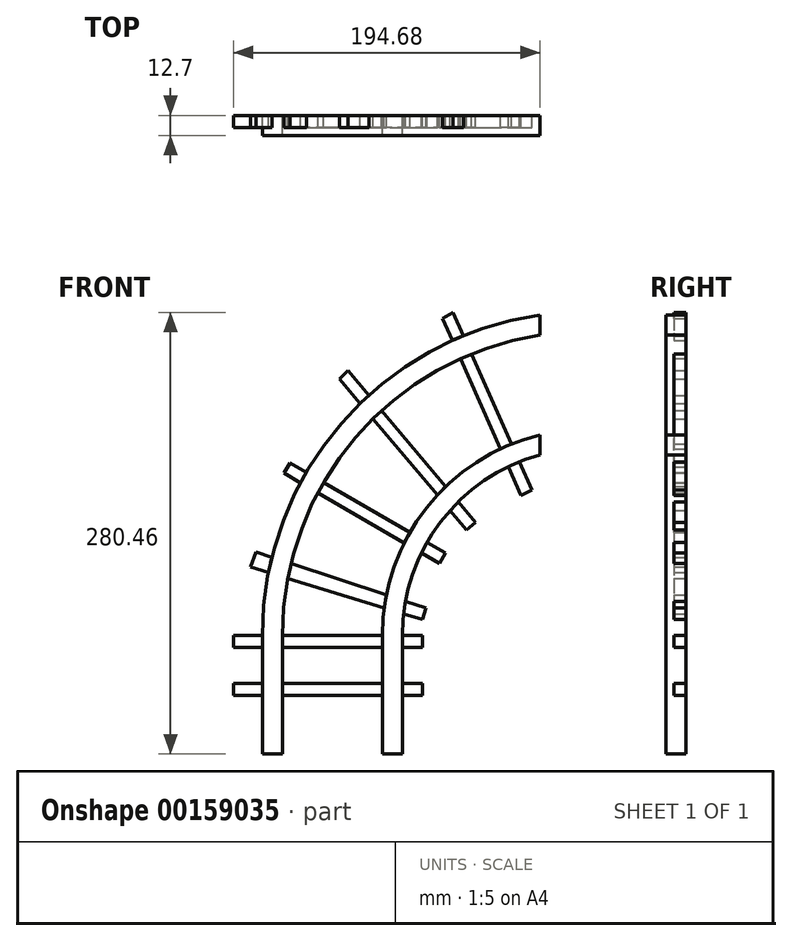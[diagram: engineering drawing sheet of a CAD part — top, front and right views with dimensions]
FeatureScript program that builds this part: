
annotation { "Feature Type Name" : "Feature", "Feature Type Description" : "" }
export const myFeature = defineFeature(function(context is Context, id is Id, definition is map)
    precondition{}
    {
        {
            var Q0;
            Q0=qCreatedBy(makeId("Front.planeOp"),FACE);
            var sketch = newSketch(context, id + "F0", { "sketchPlane" : qUnion([Q0])});
            skLineSegment(sketch, "E0", {"start": v(-53.08, 0) * mm, "end": v(-40.38, 0) * mm});
            skLineSegment(sketch, "E1", {"start": v(-40.38, 0) * mm, "end": v(-40.38, -75.5) * mm});
            skLineSegment(sketch, "E2", {"start": v(-40.38, -75.5) * mm, "end": v(-53.08, -75.5) * mm});
            skLineSegment(sketch, "E3", {"start": v(-53.08, -75.5) * mm, "end": v(-53.08, 0) * mm});
            skLineSegment(sketch, "E4", {"start": v(23.12, 0) * mm, "end": v(35.82, 0) * mm});
            skLineSegment(sketch, "E5", {"start": v(35.82, 0) * mm, "end": v(35.82, -75.5) * mm});
            skLineSegment(sketch, "E6", {"start": v(35.82, -75.5) * mm, "end": v(23.12, -75.5) * mm});
            skLineSegment(sketch, "E7", {"start": v(23.12, -75.5) * mm, "end": v(23.12, 0) * mm});
            skArc(sketch, "E8", {"start": v(123.26, 114.48) * mm, "mid": v(60.18, 72.03) * mm, "end": v(35.82, 0) * mm});
            skArc(sketch, "E9", {"start": v(123.26, 127.18) * mm, "mid": v(51.16, 80.94) * mm, "end": v(23.12, 0) * mm});
            skArc(sketch, "E10", {"start": v(123.26, 190.68) * mm, "mid": v(6.14, 125.64) * mm, "end": v(-40.38, 0) * mm});
            skArc(sketch, "E11", {"start": v(123.26, 203.38) * mm, "mid": v(-2.85, 134.6) * mm, "end": v(-53.08, 0) * mm});
            skLineSegment(sketch, "E12", {"start": v(123.26, 203.38) * mm, "end": v(123.26, 190.68) * mm});
            skLineSegment(sketch, "E13", {"start": v(123.26, 127.18) * mm, "end": v(123.26, 114.48) * mm});
            skLineSegment(sketch, "E14", {"start": v(-71.42, -30.48) * mm, "end": v(-71.42, -38.1) * mm});
            skLineSegment(sketch, "E15", {"start": v(-71.42, -38.1) * mm, "end": v(48.77, -38.1) * mm});
            skLineSegment(sketch, "E16", {"start": v(48.77, -38.1) * mm, "end": v(48.77, -30.48) * mm});
            skLineSegment(sketch, "E17", {"start": v(48.77, -30.48) * mm, "end": v(-71.42, -30.48) * mm});
            skLineSegment(sketch, "E18", {"start": v(-71.42, 0) * mm, "end": v(-71.42, -7.62) * mm});
            skLineSegment(sketch, "E19", {"start": v(-71.42, -7.62) * mm, "end": v(48.77, -7.62) * mm});
            skLineSegment(sketch, "E20", {"start": v(48.77, -7.62) * mm, "end": v(48.77, 0) * mm});
            skLineSegment(sketch, "E21", {"start": v(48.77, 0) * mm, "end": v(-71.42, 0) * mm});
            skLineSegment(sketch, "E22", {"start": v(-57.02, 52.83) * mm, "end": v(-60.61, 43.26) * mm});
            skLineSegment(sketch, "E23", {"start": v(-60.61, 43.26) * mm, "end": v(48.67, 9.97) * mm});
            skLineSegment(sketch, "E24", {"start": v(48.67, 9.97) * mm, "end": v(50.89, 17.26) * mm});
            skLineSegment(sketch, "E25", {"start": v(-57.02, 52.83) * mm, "end": v(50.89, 17.26) * mm});
            skLineSegment(sketch, "E26", {"start": v(-35.6, 109.54) * mm, "end": v(-39.43, 102.95) * mm});
            skLineSegment(sketch, "E27", {"start": v(-39.43, 102.95) * mm, "end": v(59.36, 45.68) * mm});
            skLineSegment(sketch, "E28", {"start": v(59.36, 45.68) * mm, "end": v(63.18, 52.28) * mm});
            skLineSegment(sketch, "E29", {"start": v(63.18, 52.28) * mm, "end": v(-35.6, 109.54) * mm});
            skLineSegment(sketch, "E30", {"start": v(-4.06, 162.77) * mm, "end": v(1.23, 168.25) * mm});
            skLineSegment(sketch, "E31", {"start": v(-4.06, 162.77) * mm, "end": v(76.6, 66.78) * mm});
            skLineSegment(sketch, "E32", {"start": v(76.6, 66.78) * mm, "end": v(82.43, 71.69) * mm});
            skLineSegment(sketch, "E33", {"start": v(82.43, 71.69) * mm, "end": v(1.23, 168.25) * mm});
            skLineSegment(sketch, "E34", {"start": v(61.48, 201.09) * mm, "end": v(68.05, 204.95) * mm});
            skLineSegment(sketch, "E35", {"start": v(68.05, 204.95) * mm, "end": v(118.1, 92.17) * mm});
            skLineSegment(sketch, "E36", {"start": v(61.48, 201.09) * mm, "end": v(111.28, 88.77) * mm});
            skLineSegment(sketch, "E37", {"start": v(111.28, 88.77) * mm, "end": v(118.1, 92.17) * mm});
            skSolve(sketch);
        }
        {
            var Q0;
            {var subQ0=sQuery(id+"F0.wireOp",EDGE,"E12");Q0=makeQuery(id+"F0.imprint","IMPRINT",FACE,{"disambiguationData":[TD([[makeQuery(id+"F0.imprint","IMPRINT",EDGE,{"derivedFrom":subQ0}),-1.0]])]});}
            var Q1;
            {var subQ0=sQuery(id+"F0.wireOp",EDGE,"E35");var subQ1=sQuery(id+"F0.wireOp",EDGE,"E10");var subQ2=makeQuery(id+"F0.imprint","INTERSECT",VERTEX,{"derivedFrom":[subQ1,subQ0]});Q1=makeQuery(id+"F0.imprint","IMPRINT",FACE,{"disambiguationData":[TD([[makeQuery(id+"F0.imprint","IMPRINT",EDGE,{"disambiguationData":[TD([[subQ2,-1.0]])],"derivedFrom":subQ1}),-1.0]])]});}
            var Q2;
            {var subQ0=sQuery(id+"F0.wireOp",EDGE,"E36");var subQ1=sQuery(id+"F0.wireOp",EDGE,"E10");var subQ2=makeQuery(id+"F0.imprint","INTERSECT",VERTEX,{"derivedFrom":[subQ1,subQ0]});Q2=makeQuery(id+"F0.imprint","IMPRINT",FACE,{"disambiguationData":[TD([[makeQuery(id+"F0.imprint","IMPRINT",EDGE,{"disambiguationData":[TD([[subQ2,-1.0]])],"derivedFrom":subQ1}),-1.0]])]});}
            var Q3;
            {var subQ0=sQuery(id+"F0.wireOp",EDGE,"E33");var subQ1=sQuery(id+"F0.wireOp",EDGE,"E10");var subQ2=makeQuery(id+"F0.imprint","INTERSECT",VERTEX,{"derivedFrom":[subQ1,subQ0]});Q3=makeQuery(id+"F0.imprint","IMPRINT",FACE,{"disambiguationData":[TD([[makeQuery(id+"F0.imprint","IMPRINT",EDGE,{"disambiguationData":[TD([[subQ2,-1.0]])],"derivedFrom":subQ1}),-1.0]])]});}
            var Q4;
            {var subQ0=sQuery(id+"F0.wireOp",EDGE,"E31");var subQ1=sQuery(id+"F0.wireOp",EDGE,"E10");var subQ2=makeQuery(id+"F0.imprint","INTERSECT",VERTEX,{"derivedFrom":[subQ1,subQ0]});Q4=makeQuery(id+"F0.imprint","IMPRINT",FACE,{"disambiguationData":[TD([[makeQuery(id+"F0.imprint","IMPRINT",EDGE,{"disambiguationData":[TD([[subQ2,-1.0]])],"derivedFrom":subQ1}),-1.0]])]});}
            var Q5;
            {var subQ0=sQuery(id+"F0.wireOp",EDGE,"E27");var subQ1=sQuery(id+"F0.wireOp",EDGE,"E10");var subQ2=makeQuery(id+"F0.imprint","INTERSECT",VERTEX,{"derivedFrom":[subQ1,subQ0]});Q5=makeQuery(id+"F0.imprint","IMPRINT",FACE,{"disambiguationData":[TD([[makeQuery(id+"F0.imprint","IMPRINT",EDGE,{"disambiguationData":[TD([[subQ2,-1.0]])],"derivedFrom":subQ1}),-1.0]])]});}
            var Q6;
            {var subQ0=sQuery(id+"F0.wireOp",EDGE,"E29");var subQ1=sQuery(id+"F0.wireOp",EDGE,"E10");var subQ2=makeQuery(id+"F0.imprint","INTERSECT",VERTEX,{"derivedFrom":[subQ1,subQ0]});Q6=makeQuery(id+"F0.imprint","IMPRINT",FACE,{"disambiguationData":[TD([[makeQuery(id+"F0.imprint","IMPRINT",EDGE,{"disambiguationData":[TD([[subQ2,-1.0]])],"derivedFrom":subQ1}),-1.0]])]});}
            var Q7;
            {var subQ0=sQuery(id+"F0.wireOp",EDGE,"E25");var subQ1=sQuery(id+"F0.wireOp",EDGE,"E10");var subQ2=makeQuery(id+"F0.imprint","INTERSECT",VERTEX,{"derivedFrom":[subQ1,subQ0]});Q7=makeQuery(id+"F0.imprint","IMPRINT",FACE,{"disambiguationData":[TD([[makeQuery(id+"F0.imprint","IMPRINT",EDGE,{"disambiguationData":[TD([[subQ2,-1.0]])],"derivedFrom":subQ1}),-1.0]])]});}
            var Q8;
            {var subQ3=sQuery(id+"F0.wireOp",EDGE,"E23");var subQ5=sQuery(id+"F0.wireOp",EDGE,"E11");var subQ7=makeQuery(id+"F0.imprint","INTERSECT",VERTEX,{"derivedFrom":[subQ5,subQ3]});Q8=makeQuery(id+"F0.imprint","IMPRINT",FACE,{"disambiguationData":[TD([[makeQuery(id+"F0.imprint","IMPRINT",EDGE,{"disambiguationData":[TD([[subQ7,-1.0]])],"derivedFrom":subQ3}),-1.0]])]});}
            var Q9;
            {var subQ3=sQuery(id+"F0.wireOp",EDGE,"E19");var subQ5=sQuery(id+"F0.wireOp",EDGE,"E3");var subQ6=makeQuery(id+"F0.imprint","INTERSECT",VERTEX,{"derivedFrom":[subQ5,subQ3]});Q9=makeQuery(id+"F0.imprint","IMPRINT",FACE,{"disambiguationData":[TD([[makeQuery(id+"F0.imprint","IMPRINT",EDGE,{"disambiguationData":[TD([[subQ6,-1.0]])],"derivedFrom":subQ3}),1.0]])]});}
            var Q10;
            {var subQ0=sQuery(id+"F0.wireOp",EDGE,"E19");var subQ1=sQuery(id+"F0.wireOp",EDGE,"E1");var subQ2=makeQuery(id+"F0.imprint","INTERSECT",VERTEX,{"derivedFrom":[subQ1,subQ0]});Q10=makeQuery(id+"F0.imprint","IMPRINT",FACE,{"disambiguationData":[TD([[makeQuery(id+"F0.imprint","IMPRINT",EDGE,{"disambiguationData":[TD([[subQ2,-1.0]])],"derivedFrom":subQ1}),-1.0]])]});}
            var Q11;
            {var subQ0=sQuery(id+"F0.wireOp",EDGE,"E15");var subQ1=sQuery(id+"F0.wireOp",EDGE,"E1");var subQ2=makeQuery(id+"F0.imprint","INTERSECT",VERTEX,{"derivedFrom":[subQ1,subQ0]});Q11=makeQuery(id+"F0.imprint","IMPRINT",FACE,{"disambiguationData":[TD([[makeQuery(id+"F0.imprint","IMPRINT",EDGE,{"disambiguationData":[TD([[subQ2,1.0]])],"derivedFrom":subQ1}),-1.0]])]});}
            var Q12;
            {var subQ0=sQuery(id+"F0.wireOp",EDGE,"E2");Q12=makeQuery(id+"F0.imprint","IMPRINT",FACE,{"disambiguationData":[TD([[makeQuery(id+"F0.imprint","IMPRINT",EDGE,{"derivedFrom":subQ0}),-1.0]])]});}
            var Q13;
            {var subQ0=sQuery(id+"F0.wireOp",EDGE,"E6");Q13=makeQuery(id+"F0.imprint","IMPRINT",FACE,{"disambiguationData":[TD([[makeQuery(id+"F0.imprint","IMPRINT",EDGE,{"derivedFrom":subQ0}),-1.0]])]});}
            var Q14;
            {var subQ0=sQuery(id+"F0.wireOp",EDGE,"E17");var subQ1=sQuery(id+"F0.wireOp",EDGE,"E5");var subQ2=makeQuery(id+"F0.imprint","INTERSECT",VERTEX,{"derivedFrom":[subQ1,subQ0]});Q14=makeQuery(id+"F0.imprint","IMPRINT",FACE,{"disambiguationData":[TD([[makeQuery(id+"F0.imprint","IMPRINT",EDGE,{"disambiguationData":[TD([[subQ2,-1.0]])],"derivedFrom":subQ1}),-1.0]])]});}
            var Q15;
            {var subQ0=sQuery(id+"F0.wireOp",EDGE,"E19");var subQ1=sQuery(id+"F0.wireOp",EDGE,"E5");var subQ2=makeQuery(id+"F0.imprint","INTERSECT",VERTEX,{"derivedFrom":[subQ1,subQ0]});Q15=makeQuery(id+"F0.imprint","IMPRINT",FACE,{"disambiguationData":[TD([[makeQuery(id+"F0.imprint","IMPRINT",EDGE,{"disambiguationData":[TD([[subQ2,-1.0]])],"derivedFrom":subQ1}),-1.0]])]});}
            var Q16;
            {var subQ1=sQuery(id+"F0.wireOp",EDGE,"E5");var subQ3=sQuery(id+"F0.wireOp",EDGE,"E19");var subQ4=makeQuery(id+"F0.imprint","INTERSECT",VERTEX,{"derivedFrom":[subQ1,subQ3]});Q16=makeQuery(id+"F0.imprint","IMPRINT",FACE,{"disambiguationData":[TD([[makeQuery(id+"F0.imprint","IMPRINT",EDGE,{"disambiguationData":[TD([[subQ4,1.0]])],"derivedFrom":subQ3}),1.0]])]});}
            var Q17;
            {var subQ1=sQuery(id+"F0.wireOp",EDGE,"E8");var subQ3=sQuery(id+"F0.wireOp",EDGE,"E23");var subQ4=makeQuery(id+"F0.imprint","INTERSECT",VERTEX,{"derivedFrom":[subQ1,subQ3]});Q17=makeQuery(id+"F0.imprint","IMPRINT",FACE,{"disambiguationData":[TD([[makeQuery(id+"F0.imprint","IMPRINT",EDGE,{"disambiguationData":[TD([[subQ4,1.0]])],"derivedFrom":subQ3}),-1.0]])]});}
            var Q18;
            {var subQ0=sQuery(id+"F0.wireOp",EDGE,"E25");var subQ1=sQuery(id+"F0.wireOp",EDGE,"E8");var subQ2=makeQuery(id+"F0.imprint","INTERSECT",VERTEX,{"derivedFrom":[subQ1,subQ0]});Q18=makeQuery(id+"F0.imprint","IMPRINT",FACE,{"disambiguationData":[TD([[makeQuery(id+"F0.imprint","IMPRINT",EDGE,{"disambiguationData":[TD([[subQ2,-1.0]])],"derivedFrom":subQ1}),-1.0]])]});}
            var Q19;
            {var subQ0=sQuery(id+"F0.wireOp",EDGE,"E27");var subQ1=sQuery(id+"F0.wireOp",EDGE,"E8");var subQ2=makeQuery(id+"F0.imprint","INTERSECT",VERTEX,{"derivedFrom":[subQ1,subQ0]});Q19=makeQuery(id+"F0.imprint","IMPRINT",FACE,{"disambiguationData":[TD([[makeQuery(id+"F0.imprint","IMPRINT",EDGE,{"disambiguationData":[TD([[subQ2,-1.0]])],"derivedFrom":subQ1}),-1.0]])]});}
            var Q20;
            {var subQ0=sQuery(id+"F0.wireOp",EDGE,"E29");var subQ1=sQuery(id+"F0.wireOp",EDGE,"E8");var subQ2=makeQuery(id+"F0.imprint","INTERSECT",VERTEX,{"derivedFrom":[subQ1,subQ0]});Q20=makeQuery(id+"F0.imprint","IMPRINT",FACE,{"disambiguationData":[TD([[makeQuery(id+"F0.imprint","IMPRINT",EDGE,{"disambiguationData":[TD([[subQ2,-1.0]])],"derivedFrom":subQ1}),-1.0]])]});}
            var Q21;
            {var subQ0=sQuery(id+"F0.wireOp",EDGE,"E31");var subQ1=sQuery(id+"F0.wireOp",EDGE,"E8");var subQ2=makeQuery(id+"F0.imprint","INTERSECT",VERTEX,{"derivedFrom":[subQ1,subQ0]});Q21=makeQuery(id+"F0.imprint","IMPRINT",FACE,{"disambiguationData":[TD([[makeQuery(id+"F0.imprint","IMPRINT",EDGE,{"disambiguationData":[TD([[subQ2,-1.0]])],"derivedFrom":subQ1}),-1.0]])]});}
            var Q22;
            {var subQ0=sQuery(id+"F0.wireOp",EDGE,"E33");var subQ1=sQuery(id+"F0.wireOp",EDGE,"E8");var subQ2=makeQuery(id+"F0.imprint","INTERSECT",VERTEX,{"derivedFrom":[subQ1,subQ0]});Q22=makeQuery(id+"F0.imprint","IMPRINT",FACE,{"disambiguationData":[TD([[makeQuery(id+"F0.imprint","IMPRINT",EDGE,{"disambiguationData":[TD([[subQ2,-1.0]])],"derivedFrom":subQ1}),-1.0]])]});}
            var Q23;
            {var subQ0=sQuery(id+"F0.wireOp",EDGE,"E36");var subQ1=sQuery(id+"F0.wireOp",EDGE,"E8");var subQ2=makeQuery(id+"F0.imprint","INTERSECT",VERTEX,{"derivedFrom":[subQ1,subQ0]});Q23=makeQuery(id+"F0.imprint","IMPRINT",FACE,{"disambiguationData":[TD([[makeQuery(id+"F0.imprint","IMPRINT",EDGE,{"disambiguationData":[TD([[subQ2,-1.0]])],"derivedFrom":subQ1}),-1.0]])]});}
            var Q24;
            {var subQ0=sQuery(id+"F0.wireOp",EDGE,"E35");var subQ1=sQuery(id+"F0.wireOp",EDGE,"E8");var subQ2=makeQuery(id+"F0.imprint","INTERSECT",VERTEX,{"derivedFrom":[subQ1,subQ0]});Q24=makeQuery(id+"F0.imprint","IMPRINT",FACE,{"disambiguationData":[TD([[makeQuery(id+"F0.imprint","IMPRINT",EDGE,{"disambiguationData":[TD([[subQ2,-1.0]])],"derivedFrom":subQ1}),-1.0]])]});}
            var Q25;
            {var subQ0=sQuery(id+"F0.wireOp",EDGE,"E13");Q25=makeQuery(id+"F0.imprint","IMPRINT",FACE,{"disambiguationData":[TD([[makeQuery(id+"F0.imprint","IMPRINT",EDGE,{"derivedFrom":subQ0}),-1.0]])]});}
            extrude(context, id + "F1", {"entities" : qUnion([Q0, Q1, Q2, Q3, Q4, Q5, Q6, Q7, Q8, Q9, Q10, Q11, Q12, Q13, Q14, Q15, Q16, Q17, Q18, Q19, Q20, Q21, Q22, Q23, Q24, Q25]), "depth" : 12.7 * mm});
        }
        {
            var Q0;
            {var subQ0=sQuery(id+"F0.wireOp",EDGE,"E35");var subQ1=sQuery(id+"F0.wireOp",EDGE,"E9");var subQ2=makeQuery(id+"F0.imprint","INTERSECT",VERTEX,{"derivedFrom":[subQ1,subQ0]});Q0=makeQuery(id+"F0.imprint","IMPRINT",FACE,{"disambiguationData":[TD([[makeQuery(id+"F0.imprint","IMPRINT",EDGE,{"disambiguationData":[TD([[subQ2,-1.0]])],"derivedFrom":subQ1}),-1.0]])]});}
            var Q1;
            {var subQ0=sQuery(id+"F0.wireOp",EDGE,"E33");var subQ1=sQuery(id+"F0.wireOp",EDGE,"E9");var subQ2=makeQuery(id+"F0.imprint","INTERSECT",VERTEX,{"derivedFrom":[subQ1,subQ0]});Q1=makeQuery(id+"F0.imprint","IMPRINT",FACE,{"disambiguationData":[TD([[makeQuery(id+"F0.imprint","IMPRINT",EDGE,{"disambiguationData":[TD([[subQ2,-1.0]])],"derivedFrom":subQ1}),-1.0]])]});}
            var Q2;
            {var subQ0=sQuery(id+"F0.wireOp",EDGE,"E29");var subQ1=sQuery(id+"F0.wireOp",EDGE,"E9");var subQ2=makeQuery(id+"F0.imprint","INTERSECT",VERTEX,{"derivedFrom":[subQ1,subQ0]});Q2=makeQuery(id+"F0.imprint","IMPRINT",FACE,{"disambiguationData":[TD([[makeQuery(id+"F0.imprint","IMPRINT",EDGE,{"disambiguationData":[TD([[subQ2,-1.0]])],"derivedFrom":subQ1}),-1.0]])]});}
            var Q3;
            {var subQ0=sQuery(id+"F0.wireOp",EDGE,"E25");var subQ1=sQuery(id+"F0.wireOp",EDGE,"E9");var subQ2=makeQuery(id+"F0.imprint","INTERSECT",VERTEX,{"derivedFrom":[subQ1,subQ0]});Q3=makeQuery(id+"F0.imprint","IMPRINT",FACE,{"disambiguationData":[TD([[makeQuery(id+"F0.imprint","IMPRINT",EDGE,{"disambiguationData":[TD([[subQ2,-1.0]])],"derivedFrom":subQ1}),-1.0]])]});}
            var Q4;
            {var subQ1=sQuery(id+"F0.wireOp",EDGE,"E1");var subQ3=sQuery(id+"F0.wireOp",EDGE,"E19");var subQ4=makeQuery(id+"F0.imprint","INTERSECT",VERTEX,{"derivedFrom":[subQ1,subQ3]});Q4=makeQuery(id+"F0.imprint","IMPRINT",FACE,{"disambiguationData":[TD([[makeQuery(id+"F0.imprint","IMPRINT",EDGE,{"disambiguationData":[TD([[subQ4,-1.0]])],"derivedFrom":subQ3}),1.0]])]});}
            var Q5;
            {var subQ0=sQuery(id+"F0.wireOp",EDGE,"E15");var subQ1=sQuery(id+"F0.wireOp",EDGE,"E1");var subQ2=makeQuery(id+"F0.imprint","INTERSECT",VERTEX,{"derivedFrom":[subQ1,subQ0]});Q5=makeQuery(id+"F0.imprint","IMPRINT",FACE,{"disambiguationData":[TD([[makeQuery(id+"F0.imprint","IMPRINT",EDGE,{"disambiguationData":[TD([[subQ2,1.0]])],"derivedFrom":subQ1}),1.0]])]});}
            var Q6;
            {var subQ5=sQuery(id+"F0.wireOp",EDGE,"E16");Q6=makeQuery(id+"F0.imprint","IMPRINT",FACE,{"disambiguationData":[TD([[makeQuery(id+"F0.imprint","IMPRINT",EDGE,{"derivedFrom":subQ5}),1.0]])]});}
            var Q7;
            {var subQ5=sQuery(id+"F0.wireOp",EDGE,"E20");Q7=makeQuery(id+"F0.imprint","IMPRINT",FACE,{"disambiguationData":[TD([[makeQuery(id+"F0.imprint","IMPRINT",EDGE,{"derivedFrom":subQ5}),1.0]])]});}
            var Q8;
            {var subQ5=sQuery(id+"F0.wireOp",EDGE,"E24");Q8=makeQuery(id+"F0.imprint","IMPRINT",FACE,{"disambiguationData":[TD([[makeQuery(id+"F0.imprint","IMPRINT",EDGE,{"derivedFrom":subQ5}),1.0]])]});}
            var Q9;
            {var subQ5=sQuery(id+"F0.wireOp",EDGE,"E28");Q9=makeQuery(id+"F0.imprint","IMPRINT",FACE,{"disambiguationData":[TD([[makeQuery(id+"F0.imprint","IMPRINT",EDGE,{"derivedFrom":subQ5}),1.0]])]});}
            var Q10;
            {var subQ5=sQuery(id+"F0.wireOp",EDGE,"E32");Q10=makeQuery(id+"F0.imprint","IMPRINT",FACE,{"disambiguationData":[TD([[makeQuery(id+"F0.imprint","IMPRINT",EDGE,{"derivedFrom":subQ5}),1.0]])]});}
            var Q11;
            {var subQ5=sQuery(id+"F0.wireOp",EDGE,"E37");Q11=makeQuery(id+"F0.imprint","IMPRINT",FACE,{"disambiguationData":[TD([[makeQuery(id+"F0.imprint","IMPRINT",EDGE,{"derivedFrom":subQ5}),1.0]])]});}
            var Q12;
            {var subQ5=sQuery(id+"F0.wireOp",EDGE,"E34");Q12=makeQuery(id+"F0.imprint","IMPRINT",FACE,{"disambiguationData":[TD([[makeQuery(id+"F0.imprint","IMPRINT",EDGE,{"derivedFrom":subQ5}),-1.0]])]});}
            var Q13;
            {var subQ5=sQuery(id+"F0.wireOp",EDGE,"E30");Q13=makeQuery(id+"F0.imprint","IMPRINT",FACE,{"disambiguationData":[TD([[makeQuery(id+"F0.imprint","IMPRINT",EDGE,{"derivedFrom":subQ5}),-1.0]])]});}
            var Q14;
            {var subQ5=sQuery(id+"F0.wireOp",EDGE,"E26");Q14=makeQuery(id+"F0.imprint","IMPRINT",FACE,{"disambiguationData":[TD([[makeQuery(id+"F0.imprint","IMPRINT",EDGE,{"derivedFrom":subQ5}),1.0]])]});}
            var Q15;
            {var subQ5=sQuery(id+"F0.wireOp",EDGE,"E22");Q15=makeQuery(id+"F0.imprint","IMPRINT",FACE,{"disambiguationData":[TD([[makeQuery(id+"F0.imprint","IMPRINT",EDGE,{"derivedFrom":subQ5}),1.0]])]});}
            var Q16;
            {var subQ5=sQuery(id+"F0.wireOp",EDGE,"E18");Q16=makeQuery(id+"F0.imprint","IMPRINT",FACE,{"disambiguationData":[TD([[makeQuery(id+"F0.imprint","IMPRINT",EDGE,{"derivedFrom":subQ5}),1.0]])]});}
            var Q17;
            {var subQ5=sQuery(id+"F0.wireOp",EDGE,"E14");Q17=makeQuery(id+"F0.imprint","IMPRINT",FACE,{"disambiguationData":[TD([[makeQuery(id+"F0.imprint","IMPRINT",EDGE,{"derivedFrom":subQ5}),1.0]])]});}
            extrude(context, id + "F2", {"entities" : qUnion([Q0, Q1, Q2, Q3, Q4, Q5, Q6, Q7, Q8, Q9, Q10, Q11, Q12, Q13, Q14, Q15, Q16, Q17]), "depth" : 7.62 * mm});
        }
    });
